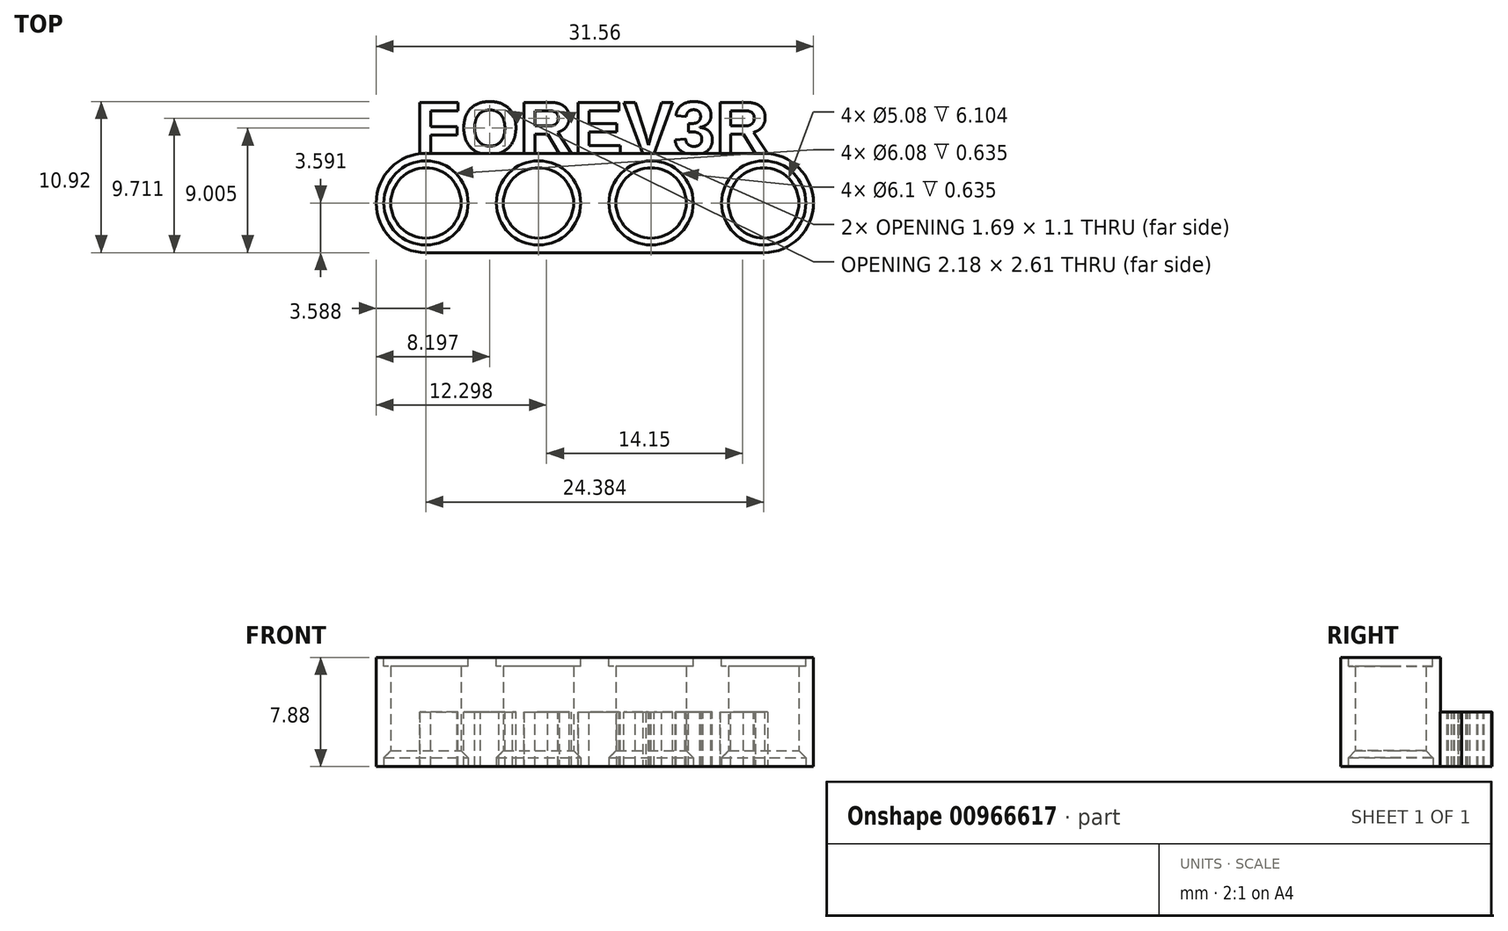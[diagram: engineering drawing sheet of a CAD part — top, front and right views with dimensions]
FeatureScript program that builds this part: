
annotation { "Feature Type Name" : "Feature", "Feature Type Description" : "" }
export const myFeature = defineFeature(function(context is Context, id is Id, definition is map)
    precondition{}
    {
        {
            var Q0;
            Q0=qCreatedBy(makeId("Top.planeOp"),FACE);
            var sketch = newSketch(context, id + "F0", { "sketchPlane" : qUnion([Q0])});
            skCircle(sketch, "E0", {"center": v(-60.84, 14.37) * mm, "radius": 3.6 * mm});
            skCircle(sketch, "E1.1.0.0", {"center": v(-52.71, 14.37) * mm, "radius": 3.6 * mm});
            skCircle(sketch, "E1.2.0.0", {"center": v(-44.59, 14.37) * mm, "radius": 3.6 * mm});
            skCircle(sketch, "E1.3.0.0", {"center": v(-36.46, 14.37) * mm, "radius": 3.6 * mm});
            skLineSegment(sketch, "E1.direction1", {"start": v(-60.84, 14.37) * mm, "end": v(-52.71, 14.37) * mm, "construction": true});
            skLineSegment(sketch, "E2.left", {"start": v(-60.84, 14.37) * mm, "end": v(-60.84, 14.37) * mm});
            skCircle(sketch, "E3", {"center": v(-60.84, 14.37) * mm, "radius": 3.05 * mm});
            skCircle(sketch, "E4.1.0.0", {"center": v(-52.71, 14.37) * mm, "radius": 3.05 * mm});
            skCircle(sketch, "E4.2.0.0", {"center": v(-44.59, 14.37) * mm, "radius": 3.05 * mm});
            skCircle(sketch, "E4.3.0.0", {"center": v(-36.46, 14.37) * mm, "radius": 3.05 * mm});
            skCircle(sketch, "E5", {"center": v(-60.84, 14.37) * mm, "radius": 2.54 * mm});
            skCircle(sketch, "E6.1.0.0", {"center": v(-52.71, 14.37) * mm, "radius": 2.54 * mm});
            skCircle(sketch, "E6.2.0.0", {"center": v(-44.59, 14.37) * mm, "radius": 2.54 * mm});
            skCircle(sketch, "E6.3.0.0", {"center": v(-36.46, 14.37) * mm, "radius": 2.54 * mm});
            skLineSegment(sketch, "E7", {"start": v(-60.84, 10.78) * mm, "end": v(-36.46, 10.78) * mm});
            skLineSegment(sketch, "E8", {"start": v(-60.84, 17.96) * mm, "end": v(-36.46, 17.96) * mm});
            skSolve(sketch);
        }
        {
            var Q0;
            Q0=makeQuery(id+"F0.imprint","IMPRINT",FACE,{"disambiguationData":[TD([[makeQuery(id+"F0.imprint","IMPRINT",EDGE,{"derivedFrom":sQuery(id+"F0.wireOp",EDGE,"E4.2.0.0")}),1.0]])]});
            var Q1;
            {var subQ0=sQuery(id+"F0.wireOp",EDGE,"wCOvyQ4Y-cXof-9WCH-Gvol-uzIAEfhHK9gS.bottom");var subQ1=sQuery(id+"F0.wireOp",EDGE,"E0");var subQ2=makeQuery(id+"F0.imprint","INTERSECT",VERTEX,{"derivedFrom":[subQ1,subQ0]});Q1=makeQuery(id+"F0.imprint","IMPRINT",FACE,{"disambiguationData":[TD([[makeQuery(id+"F0.imprint","IMPRINT",EDGE,{"disambiguationData":[TD([[subQ2,1.0]])],"derivedFrom":subQ1}),-1.0]])]});}
            var Q2;
            {var subQ0=sQuery(id+"F0.wireOp",EDGE,"wCOvyQ4Y-cXof-9WCH-Gvol-uzIAEfhHK9gS.bottom");var subQ1=sQuery(id+"F0.wireOp",EDGE,"E1.1.0.0");var subQ2=makeQuery(id+"F0.imprint","INTERSECT",VERTEX,{"derivedFrom":[subQ1,subQ0]});Q2=makeQuery(id+"F0.imprint","IMPRINT",FACE,{"disambiguationData":[TD([[makeQuery(id+"F0.imprint","IMPRINT",EDGE,{"disambiguationData":[TD([[subQ2,1.0]])],"derivedFrom":subQ1}),-1.0]])]});}
            var Q3;
            Q3=makeQuery(id+"F0.imprint","IMPRINT",FACE,{"disambiguationData":[TD([[makeQuery(id+"F0.imprint","IMPRINT",EDGE,{"derivedFrom":sQuery(id+"F0.wireOp",EDGE,"E4.2.0.0")}),-1.0]])]});
            var Q4;
            Q4=makeQuery(id+"F0.imprint","IMPRINT",FACE,{"disambiguationData":[TD([[makeQuery(id+"F0.imprint","IMPRINT",EDGE,{"derivedFrom":sQuery(id+"F0.wireOp",EDGE,"E4.1.0.0")}),-1.0]])]});
            var Q5;
            Q5=makeQuery(id+"F0.imprint","IMPRINT",FACE,{"disambiguationData":[TD([[makeQuery(id+"F0.imprint","IMPRINT",EDGE,{"derivedFrom":sQuery(id+"F0.wireOp",EDGE,"E4.3.0.0")}),-1.0]])]});
            var Q6;
            Q6=makeQuery(id+"F0.imprint","IMPRINT",FACE,{"disambiguationData":[TD([[makeQuery(id+"F0.imprint","IMPRINT",EDGE,{"derivedFrom":sQuery(id+"F0.wireOp",EDGE,"E4.3.0.0")}),1.0]])]});
            var Q7;
            {var subQ0=sQuery(id+"F0.wireOp",EDGE,"wCOvyQ4Y-cXof-9WCH-Gvol-uzIAEfhHK9gS.bottom");var subQ1=sQuery(id+"F0.wireOp",EDGE,"E1.3.0.0");var subQ2=makeQuery(id+"F0.imprint","INTERSECT",VERTEX,{"derivedFrom":[subQ1,subQ0]});Q7=makeQuery(id+"F0.imprint","IMPRINT",FACE,{"disambiguationData":[TD([[makeQuery(id+"F0.imprint","IMPRINT",EDGE,{"disambiguationData":[TD([[subQ2,1.0]])],"derivedFrom":subQ1}),-1.0]])]});}
            var Q8;
            Q8=makeQuery(id+"F0.imprint","IMPRINT",FACE,{"disambiguationData":[TD([[makeQuery(id+"F0.imprint","IMPRINT",EDGE,{"derivedFrom":sQuery(id+"F0.wireOp",EDGE,"E4.4.0.0")}),-1.0]])]});
            var Q9;
            Q9=makeQuery(id+"F0.imprint","IMPRINT",FACE,{"disambiguationData":[TD([[makeQuery(id+"F0.imprint","IMPRINT",EDGE,{"derivedFrom":sQuery(id+"F0.wireOp",EDGE,"E4.1.0.0")}),1.0]])]});
            var Q10;
            {var subQ0=sQuery(id+"F0.wireOp",EDGE,"wCOvyQ4Y-cXof-9WCH-Gvol-uzIAEfhHK9gS.bottom");var subQ1=sQuery(id+"F0.wireOp",EDGE,"E1.2.0.0");var subQ2=makeQuery(id+"F0.imprint","INTERSECT",VERTEX,{"derivedFrom":[subQ1,subQ0]});Q10=makeQuery(id+"F0.imprint","IMPRINT",FACE,{"disambiguationData":[TD([[makeQuery(id+"F0.imprint","IMPRINT",EDGE,{"disambiguationData":[TD([[subQ2,1.0]])],"derivedFrom":subQ1}),-1.0]])]});}
            var Q11;
            Q11=makeQuery(id+"F0.imprint","IMPRINT",FACE,{"disambiguationData":[TD([[makeQuery(id+"F0.imprint","IMPRINT",EDGE,{"derivedFrom":sQuery(id+"F0.wireOp",EDGE,"E4.4.0.0")}),1.0]])]});
            var Q12;
            Q12=makeQuery(id+"F0.imprint","IMPRINT",FACE,{"disambiguationData":[TD([[makeQuery(id+"F0.imprint","IMPRINT",EDGE,{"derivedFrom":sQuery(id+"F0.wireOp",EDGE,"E3")}),-1.0]])]});
            var Q13;
            Q13=makeQuery(id+"F0.imprint","IMPRINT",FACE,{"disambiguationData":[TD([[makeQuery(id+"F0.imprint","IMPRINT",EDGE,{"derivedFrom":sQuery(id+"F0.wireOp",EDGE,"E3")}),1.0]])]});
            extrude(context, id + "F1", {"entities" : qUnion([Q0, Q1, Q2, Q3, Q4, Q5, Q6, Q7, Q8, Q9, Q10, Q11, Q12, Q13]), "endBound" : BoundingType.SYMMETRIC, "depth" : 7.87 * mm});
        }
        {
            var Q0;
            Q0=makeQuery(id+"F1.opExtrude","CAP_FACE",FACE,{"disambiguationData":[OSD([sQuery(id+"F0.wireOp",EDGE,"E0"),sQuery(id+"F0.wireOp",EDGE,"cf1b550b-a4da-4dbf-a2b7-7c8ce7a8ddf9.0.4.0"),sQuery(id+"F0.wireOp",EDGE,"wCOvyQ4Y-cXof-9WCH-Gvol-uzIAEfhHK9gS.bottom"),sQuery(id+"F0.wireOp",EDGE,"wCOvyQ4Y-cXof-9WCH-Gvol-uzIAEfhHK9gS.top"),sQuery(id+"F0.wireOp",EDGE,"E5"),sQuery(id+"F0.wireOp",EDGE,"E6.1.0.0"),sQuery(id+"F0.wireOp",EDGE,"E6.2.0.0"),sQuery(id+"F0.wireOp",EDGE,"E6.3.0.0"),sQuery(id+"F0.wireOp",EDGE,"E6.4.0.0")])],"isStart":false});
            var sketch = newSketch(context, id + "F2", { "sketchPlane" : qUnion([Q0])});
            skCircle(sketch, "E9", {"center": v(-36.46, 14.37) * mm, "radius": 3.04 * mm});
            skCircle(sketch, "E10.1.0.0", {"center": v(-44.59, 14.37) * mm, "radius": 3.04 * mm});
            skCircle(sketch, "E10.2.0.0", {"center": v(-52.71, 14.37) * mm, "radius": 3.04 * mm});
            skLineSegment(sketch, "E10.direction1", {"start": v(-36.46, 14.37) * mm, "end": v(-44.59, 14.37) * mm, "construction": true});
            skCircle(sketch, "E11.0.3.0", {"center": v(-60.84, 14.37) * mm, "radius": 3.04 * mm});
            skSolve(sketch);
        }
        {
            var Q0;
            Q0=qSketchRegion(id+"F2",true);
            extrude(context, id + "F3", {"entities" : qUnion([Q0]), "operationType" : NewBodyOperationType.REMOVE, "oppositeDirection" : true, "offsetDistance" : 25 * mm, "depth" : 0.64 * mm});
        }
        {
            var Q0;
            Q0=makeQuery(id+"F1.opExtrude","CAP_FACE",FACE,{"disambiguationData":[OSD([sQuery(id+"F0.wireOp",EDGE,"E0"),sQuery(id+"F0.wireOp",EDGE,"cf1b550b-a4da-4dbf-a2b7-7c8ce7a8ddf9.0.4.0"),sQuery(id+"F0.wireOp",EDGE,"wCOvyQ4Y-cXof-9WCH-Gvol-uzIAEfhHK9gS.bottom"),sQuery(id+"F0.wireOp",EDGE,"wCOvyQ4Y-cXof-9WCH-Gvol-uzIAEfhHK9gS.top"),sQuery(id+"F0.wireOp",EDGE,"E5"),sQuery(id+"F0.wireOp",EDGE,"E6.1.0.0"),sQuery(id+"F0.wireOp",EDGE,"E6.2.0.0"),sQuery(id+"F0.wireOp",EDGE,"E6.3.0.0"),sQuery(id+"F0.wireOp",EDGE,"E6.4.0.0")])],"isStart":true});
            var sketch = newSketch(context, id + "F4", { "sketchPlane" : qUnion([Q0])});
            skCircle(sketch, "E12", {"center": v(-60.84, -14.37) * mm, "radius": 3.05 * mm});
            skCircle(sketch, "E13.1.0.0", {"center": v(-52.71, -14.37) * mm, "radius": 3.05 * mm});
            skCircle(sketch, "E13.2.0.0", {"center": v(-44.59, -14.37) * mm, "radius": 3.05 * mm});
            skCircle(sketch, "E13.3.0.0", {"center": v(-36.46, -14.37) * mm, "radius": 3.05 * mm});
            skLineSegment(sketch, "E13.direction1", {"start": v(-60.84, -14.37) * mm, "end": v(-52.71, -14.37) * mm, "construction": true});
            skSolve(sketch);
        }
        {
            var Q0;
            Q0=makeQuery(id+"F1.opExtrude","CAP_EDGE",EDGE,{"disambiguationData":[OSD([sQuery(id+"F0.wireOp",EDGE,"E6.3.0.0")])],"isStart":true});
            var Q1;
            Q1=makeQuery(id+"F1.opExtrude","CAP_EDGE",EDGE,{"disambiguationData":[OSD([sQuery(id+"F0.wireOp",EDGE,"E6.2.0.0")])],"isStart":true});
            var Q2;
            Q2=makeQuery(id+"F1.opExtrude","CAP_EDGE",EDGE,{"disambiguationData":[OSD([sQuery(id+"F0.wireOp",EDGE,"E6.1.0.0")])],"isStart":true});
            var Q3;
            Q3=makeQuery(id+"F1.opExtrude","CAP_EDGE",EDGE,{"disambiguationData":[OSD([sQuery(id+"F0.wireOp",EDGE,"E5")])],"isStart":true});
            chamfer(context, id + "F5", {"entities" : qUnion([Q0, Q1, Q2, Q3]), "chamferType" : ChamferType.OFFSET_ANGLE, "width" : 0.5 * mm, "oppositeDirection" : false, "angle" : 45 * degree});
        }
        {
            var Q0;
            Q0=qSketchRegion(id+"F4",true);
            extrude(context, id + "F6", {"entities" : qUnion([Q0]), "operationType" : NewBodyOperationType.REMOVE, "oppositeDirection" : true, "offsetDistance" : 25 * mm, "depth" : 0.64 * mm});
        }
        {
            var Q0;
            Q0=makeQuery(id+"F6.boolean.opBoolean","INTERSECT",EDGE,{"derivedFrom":[makeQuery(id+"F1.opExtrude","SWEPT_FACE",FACE,{"disambiguationData":[OSD([sQuery(id+"F0.wireOp",EDGE,"E6.2.0.0")])]}),makeQuery(id+"F6.opExtrude","CAP_FACE",FACE,{"disambiguationData":[OSD([sQuery(id+"F4.wireOp",EDGE,"E13.2.0.0")])],"isStart":false})]});
            var Q1;
            Q1=makeQuery(id+"F6.boolean.opBoolean","INTERSECT",EDGE,{"derivedFrom":[makeQuery(id+"F1.opExtrude","SWEPT_FACE",FACE,{"disambiguationData":[OSD([sQuery(id+"F0.wireOp",EDGE,"E6.1.0.0")])]}),makeQuery(id+"F6.opExtrude","CAP_FACE",FACE,{"disambiguationData":[OSD([sQuery(id+"F4.wireOp",EDGE,"E13.1.0.0")])],"isStart":false})]});
            var Q2;
            Q2=makeQuery(id+"F6.boolean.opBoolean","INTERSECT",EDGE,{"derivedFrom":[makeQuery(id+"F1.opExtrude","SWEPT_FACE",FACE,{"disambiguationData":[OSD([sQuery(id+"F0.wireOp",EDGE,"E5")])]}),makeQuery(id+"F6.opExtrude","CAP_FACE",FACE,{"disambiguationData":[OSD([sQuery(id+"F4.wireOp",EDGE,"E12")])],"isStart":false})]});
            var Q3;
            Q3=makeQuery(id+"F6.boolean.opBoolean","INTERSECT",EDGE,{"derivedFrom":[makeQuery(id+"F1.opExtrude","SWEPT_FACE",FACE,{"disambiguationData":[OSD([sQuery(id+"F0.wireOp",EDGE,"E6.3.0.0")])]}),makeQuery(id+"F6.opExtrude","CAP_FACE",FACE,{"disambiguationData":[OSD([sQuery(id+"F4.wireOp",EDGE,"E13.3.0.0")])],"isStart":false})]});
            chamfer(context, id + "F7", {"entities" : qUnion([Q0, Q1, Q2, Q3]), "width" : .5 * mm, "tangentPropagation" : true});
        }
        {
            var Q0;
            Q0=qCreatedBy(makeId("Top.planeOp"),FACE);
            var sketch = newSketch(context, id + "F8", { "sketchPlane" : qUnion([Q0])});
            skText(sketch, "E14", { "text": "FOREV3R", "fontName": "Arimo-Bold.ttf"});
            const initialGuessF8  = {"E14": [-0.06164, 0.01792, 1, 0, 0.0039]};
            skSetInitialGuess(sketch, initialGuessF8);
            skSolve(sketch);
        }
        {
            var Q0;
            Q0=qSketchRegion(id+"F8",true);
            extrude(context, id + "F9", {"entities" : qUnion([Q0]), "operationType" : NewBodyOperationType.ADD, "oppositeDirection" : true, "depth" : 3.94 * mm, "offsetDistance" : 25 * mm});
        }
    });
